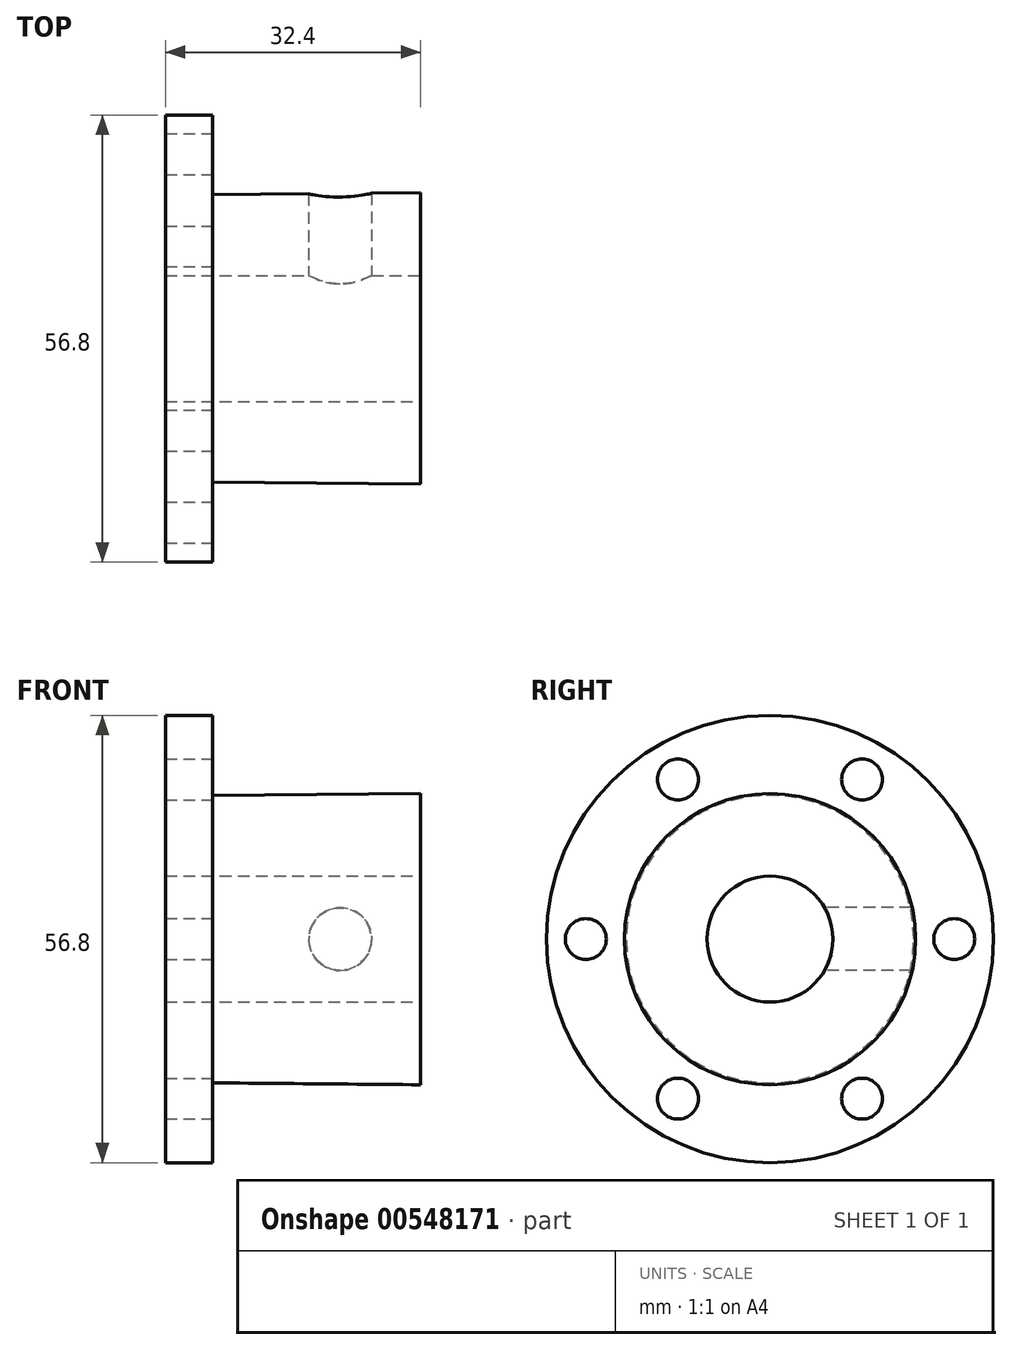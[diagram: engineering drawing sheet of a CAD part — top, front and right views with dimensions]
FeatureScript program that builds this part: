
annotation { "Feature Type Name" : "Feature", "Feature Type Description" : "" }
export const myFeature = defineFeature(function(context is Context, id is Id, definition is map)
    precondition{}
    {
        {
            var Q0;
            Q0=qCreatedBy(makeId("Front.planeOp"),FACE);
            var sketch = newSketch(context, id + "F0", { "sketchPlane" : qUnion([Q0])});
            skLineSegment(sketch, "E0", {"start": v(44.45, 0) * mm, "end": v(0, 0) * mm});
            skLineSegment(sketch, "E1", {"start": v(48.08, 18.5) * mm, "end": v(48.08, 8) * mm});
            skLineSegment(sketch, "E2", {"start": v(48.08, 8) * mm, "end": v(15.68, 8) * mm});
            skLineSegment(sketch, "E3", {"start": v(15.68, 8) * mm, "end": v(15.68, 28.4) * mm});
            skLineSegment(sketch, "E4", {"start": v(15.68, 28.4) * mm, "end": v(21.68, 28.4) * mm});
            skLineSegment(sketch, "E5", {"start": v(21.68, 28.4) * mm, "end": v(21.68, 18.26) * mm});
            skLineSegment(sketch, "E6", {"start": v(21.68, 18.26) * mm, "end": v(48.08, 18.5) * mm});
            skSolve(sketch);
        }
        {
            var Q0;
            Q0 = qSketchRegion(id + "F0", true);
            var Q1;
            Q1=sQuery(id+"F0.wireOp",EDGE,"E0");
            revolve(context, id + "F1", {"entities" : qUnion([Q0]), "axis" : qUnion([Q1]), "revolveType" : RevolveType.FULL});
        }
        {
            var Q0;
            Q0=makeQuery(id+"F1.opRevolve","SWEPT_FACE",FACE,{"disambiguationData":[OSD([sQuery(id+"F0.wireOp",EDGE,"E5")])]});
            var sketch = newSketch(context, id + "F2", { "sketchPlane" : qUnion([Q0])});
            skLineSegment(sketch, "E7", {"start": v(0, 0) * mm, "end": v(-46.8, 0) * mm, "construction": true});
            skCircle(sketch, "E8", {"center": v(-23.4, 0) * mm, "radius": 2.6 * mm});
            skCircle(sketch, "E9.1.0", {"center": v(-11.7, -20.26) * mm, "radius": 2.6 * mm});
            skCircle(sketch, "E9.2.0", {"center": v(11.7, -20.26) * mm, "radius": 2.6 * mm});
            skCircle(sketch, "E9.3.0", {"center": v(23.4, 0) * mm, "radius": 2.6 * mm});
            skCircle(sketch, "E9.4.0", {"center": v(11.7, 20.26) * mm, "radius": 2.6 * mm});
            skCircle(sketch, "E9.5.0", {"center": v(-11.7, 20.26) * mm, "radius": 2.6 * mm});
            skPoint(sketch, "E9.center", {"position": v(0, 0) * mm});
            skSolve(sketch);
        }
        {
            var Q0;
            Q0 = qSketchRegion(id + "F2", true);
            extrude(context, id + "F3", {"entities" : qUnion([Q0]), "operationType" : NewBodyOperationType.REMOVE, "oppositeDirection" : true, "depth" : 6 * mm, "offsetDistance" : 25 * mm});
        }
        {
            var Q0;
            Q0=qCreatedBy(makeId("Front.planeOp"),FACE);
            var sketch = newSketch(context, id + "F4", { "sketchPlane" : qUnion([Q0])});
            skCircle(sketch, "E10", {"center": v(37.88, 0) * mm, "radius": 4 * mm});
            skSolve(sketch);
        }
        {
            var Q0;
            Q0 = qSketchRegion(id + "F4", true);
            var Q1;
            Q1=sQuery(id+"F4.wireOp",EDGE,"E10");
            extrude(context, id + "F5", {"entities" : qUnion([Q0]), "operationType" : NewBodyOperationType.REMOVE, "surfaceEntities" : qUnion([Q1]), "endBound" : BoundingType.THROUGH_ALL, "oppositeDirection" : true, "depth" : 25 * mm, "offsetDistance" : 25 * mm});
        }
    });
